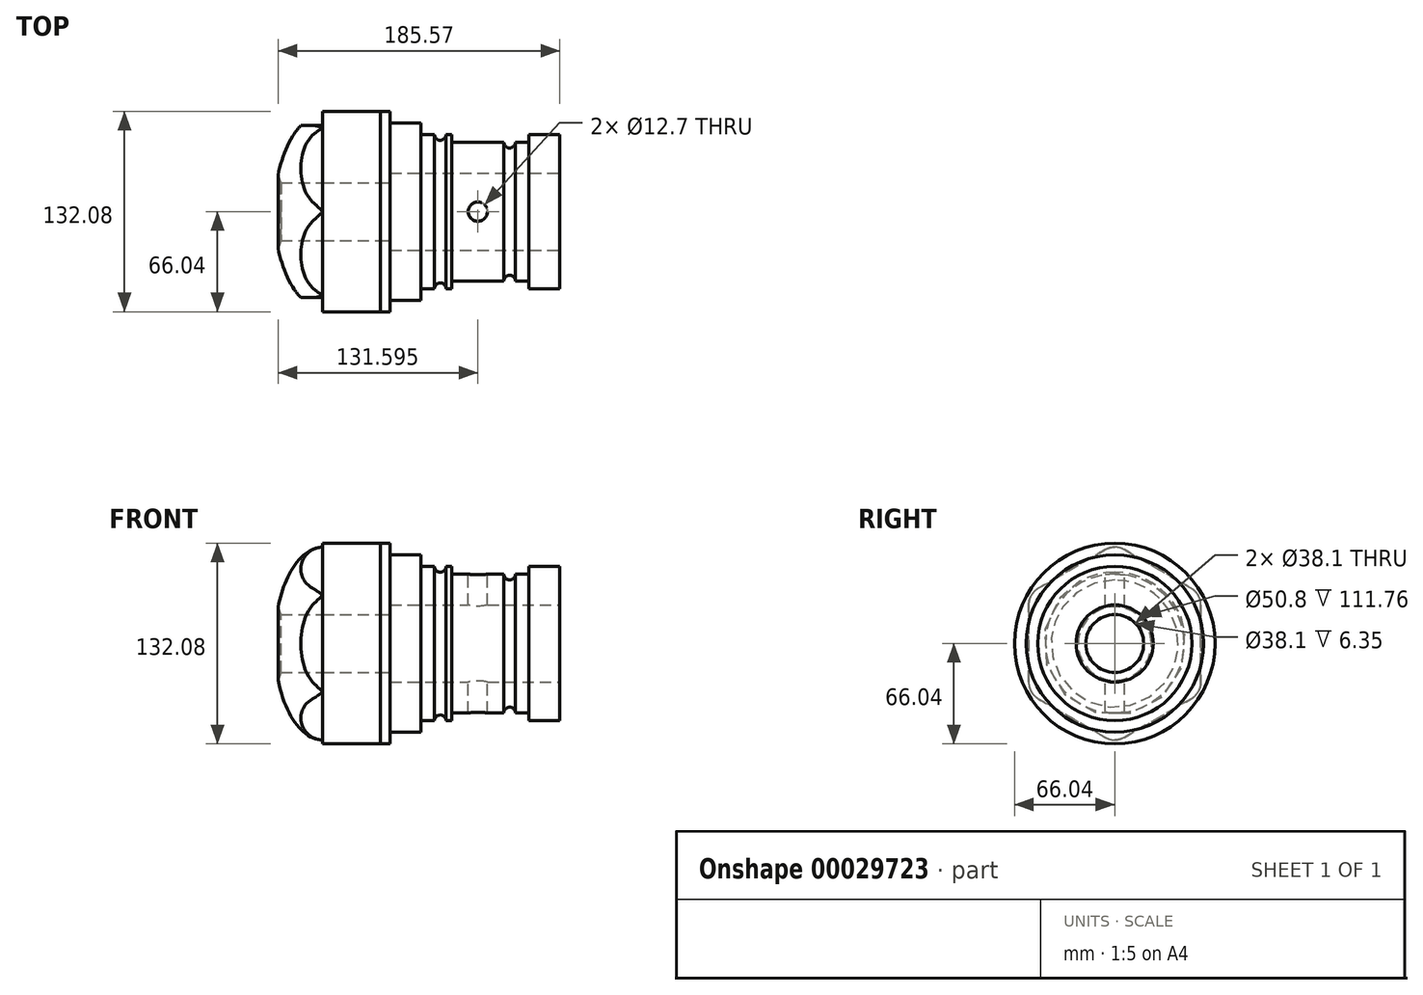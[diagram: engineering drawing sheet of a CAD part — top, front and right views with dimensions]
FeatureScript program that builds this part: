
annotation { "Feature Type Name" : "Feature", "Feature Type Description" : "" }
export const myFeature = defineFeature(function(context is Context, id is Id, definition is map)
    precondition{}
    {
        {
            var Q0;
            Q0=qCreatedBy(makeId("Top.planeOp"),FACE);
            var sketch = newSketch(context, id + "F0", { "sketchPlane" : qUnion([Q0])});
            skLineSegment(sketch, "E0", {"start": v(0, 0) * mm, "end": v(0, -50.8) * mm});
            skLineSegment(sketch, "E1", {"start": v(0, -50.8) * mm, "end": v(-20.32, -50.8) * mm});
            skLineSegment(sketch, "E2", {"start": v(-20.32, -50.8) * mm, "end": v(-20.32, -45.72) * mm});
            skLineSegment(sketch, "E3", {"start": v(-20.32, -45.72) * mm, "end": v(-29.21, -45.72) * mm});
            skLineSegment(sketch, "E4", {"start": v(-91.44, -50.8) * mm, "end": v(-91.44, -58.42) * mm});
            skLineSegment(sketch, "E5", {"start": v(-91.44, -58.42) * mm, "end": v(-111.76, -58.42) * mm});
            skLineSegment(sketch, "E6", {"start": v(-111.76, -58.42) * mm, "end": v(-111.76, -66.04) * mm});
            skLineSegment(sketch, "E7", {"start": v(-111.76, -66.04) * mm, "end": v(-118.11, -66.04) * mm});
            skLineSegment(sketch, "E8", {"start": v(-118.11, -66.04) * mm, "end": v(-118.11, 0) * mm});
            skLineSegment(sketch, "E9", {"start": v(-118.11, 0) * mm, "end": v(0, 0) * mm});
            skLineSegment(sketch, "E10", {"start": v(-91.44, -50.8) * mm, "end": v(-82.55, -50.8) * mm});
            skLineSegment(sketch, "E11", {"start": v(-71.12, -45.72) * mm, "end": v(-71.12, -50.8) * mm});
            skArc(sketch, "E12", {"start": v(-29.21, -45.72) * mm, "mid": v(-33.02, -41.9) * mm, "end": v(-36.83, -45.72) * mm});
            skArc(sketch, "E13", {"start": v(-74.93, -50.8) * mm, "mid": v(-78.74, -47) * mm, "end": v(-82.55, -50.8) * mm});
            skLineSegment(sketch, "E14.trimOffspring", {"start": v(-74.93, -50.8) * mm, "end": v(-71.12, -50.8) * mm});
            skLineSegment(sketch, "E15.trimOffspring", {"start": v(-36.83, -45.72) * mm, "end": v(-71.12, -45.72) * mm});
            skSolve(sketch);
        }
        {
            var Q0;
            Q0 = qSketchRegion(id + "F0", true);
            var Q1;
            Q1=sQuery(id+"F0.wireOp",EDGE,"E9");
            revolve(context, id + "F1", {"entities" : qUnion([Q0]), "axis" : qUnion([Q1]), "revolveType" : RevolveType.FULL});
        }
        {
            var Q0;
            Q0=makeQuery(id+"F1.opRevolve","SWEPT_FACE",FACE,{"disambiguationData":[OSD([sQuery(id+"F0.wireOp",EDGE,"E8")])]});
            var sketch = newSketch(context, id + "F2", { "sketchPlane" : qUnion([Q0])});
            skCircle(sketch, "E16.0", {"center": v(0, 0) * mm, "radius": 66.04 * mm});
            skSolve(sketch);
        }
        {
            var Q0;
            Q0 = qSketchRegion(id + "F2", true);
            extrude(context, id + "F3", {"entities" : qUnion([Q0]), "depth" : 38.1 * mm});
        }
        {
            var Q0;
            Q0=qCreatedBy(makeId("Top.planeOp"),FACE);
            var sketch = newSketch(context, id + "F4", { "sketchPlane" : qUnion([Q0])});
            skLineSegment(sketch, "E17.0", {"start": v(-156.21, -66.04) * mm, "end": v(-156.21, 0) * mm});
            skEllipticalArc(sketch, "E18", {});
            skLineSegment(sketch, "E19", {"start": v(-156.21, 0) * mm, "end": v(-187.96, 0) * mm});
            skPoint(sketch, "E20.orphan", {"position": v(-156.21, 66.04) * mm});
            const initialGuessF4  = {"E18": [-0.15621, 0, 0, -1, 0.0635, 0.03175, 4.71238898038469, 0]};
            skSetInitialGuess(sketch, initialGuessF4);
            skSolve(sketch);
        }
        {
            var Q0;
            Q0 = qSketchRegion(id + "F4", true);
            var Q1;
            Q1=sQuery(id+"F4.wireOp",EDGE,"E19");
            revolve(context, id + "F5", {"entities" : qUnion([Q0]), "axis" : qUnion([Q1]), "revolveType" : RevolveType.FULL});
        }
        {
            var Q0;
            Q0=makeQuery(id+"F3.opExtrude","CAP_FACE",FACE,{"disambiguationData":[OSD([sQuery(id+"F2.wireOp",EDGE,"E16.0")])],"isStart":false});
            var sketch = newSketch(context, id + "F6", { "sketchPlane" : qUnion([Q0])});
            skCircle(sketch, "E21.0", {"center": v(0, 0) * mm, "radius": 66.04 * mm});
            skCircle(sketch, "E22.cCircle", {"center": v(0, 0) * mm, "radius": 65.46 * mm, "construction": true});
            skLineSegment(sketch, "E22.0", {"start": v(6.35, 61.8) * mm, "end": v(50.34, 36.4) * mm});
            skLineSegment(sketch, "E22.1", {"start": v(56.7, 25.4) * mm, "end": v(56.7, -25.4) * mm});
            skLineSegment(sketch, "E22.2", {"start": v(50.34, -36.4) * mm, "end": v(6.35, -61.8) * mm});
            skLineSegment(sketch, "E22.3", {"start": v(-6.35, -61.8) * mm, "end": v(-50.34, -36.4) * mm});
            skLineSegment(sketch, "E22.4", {"start": v(-56.7, -25.4) * mm, "end": v(-56.7, 25.4) * mm});
            skLineSegment(sketch, "E22.5", {"start": v(-50.34, 36.4) * mm, "end": v(-6.35, 61.8) * mm});
            skPoint(sketch, "E23.visualSharp", {"position": v(0, 65.46) * mm});
            skArc(sketch, "E23.filletArc", {"start": v(6.35, 61.8) * mm, "mid": v(0, 63.5) * mm, "end": v(-6.35, 61.8) * mm});
            skPoint(sketch, "E24.visualSharp", {"position": v(56.7, 32.73) * mm});
            skArc(sketch, "E24.filletArc", {"start": v(56.7, 25.4) * mm, "mid": v(55, 31.75) * mm, "end": v(50.34, 36.4) * mm});
            skPoint(sketch, "E25.visualSharp", {"position": v(56.7, -32.73) * mm});
            skArc(sketch, "E25.filletArc", {"start": v(50.34, -36.4) * mm, "mid": v(55, -31.75) * mm, "end": v(56.7, -25.4) * mm});
            skPoint(sketch, "E26.visualSharp", {"position": v(0, -65.46) * mm});
            skArc(sketch, "E26.filletArc", {"start": v(-6.35, -61.8) * mm, "mid": v(0, -63.5) * mm, "end": v(6.35, -61.8) * mm});
            skPoint(sketch, "E27.visualSharp", {"position": v(-56.7, -32.73) * mm});
            skArc(sketch, "E27.filletArc", {"start": v(-56.7, -25.4) * mm, "mid": v(-55, -31.75) * mm, "end": v(-50.34, -36.4) * mm});
            skPoint(sketch, "E28.visualSharp", {"position": v(-56.7, 32.73) * mm});
            skArc(sketch, "E28.filletArc", {"start": v(-50.34, 36.4) * mm, "mid": v(-55, 31.75) * mm, "end": v(-56.7, 25.4) * mm});
            skSolve(sketch);
        }
        {
            var Q0;
            {var subQ16=sQuery(id+"F6.wireOp",EDGE,"E22.0");Q0=makeQuery(id+"F6.imprint","IMPRINT",FACE,{"disambiguationData":[TD([[makeQuery(id+"F6.imprint","IMPRINT",EDGE,{"derivedFrom":subQ16}),-1.0]])]});}
            extrude(context, id + "F7", {"entities" : qUnion([Q0]), "endBound" : BoundingType.SYMMETRIC, "depth" : 127 * mm});
        }
        {
            var Q0;
            Q0=makeQuery(id+"F5.opRevolve","SWEPT_BODY",BODY,{"disambiguationData":[OSD([sQuery(id+"F4.wireOp",EDGE,"E17.0"),sQuery(id+"F4.wireOp",EDGE,"E18"),sQuery(id+"F4.wireOp",EDGE,"E19")])]});
            var Q1;
            Q1=makeQuery(id+"F7.opExtrude","SWEPT_BODY",BODY,{"disambiguationData":[OSD([sQuery(id+"F6.wireOp",EDGE,"E22.0"),sQuery(id+"F6.wireOp",EDGE,"E22.1"),sQuery(id+"F6.wireOp",EDGE,"E22.2"),sQuery(id+"F6.wireOp",EDGE,"E22.3"),sQuery(id+"F6.wireOp",EDGE,"E22.4"),sQuery(id+"F6.wireOp",EDGE,"E22.5"),sQuery(id+"F6.wireOp",EDGE,"E23.filletArc"),sQuery(id+"F6.wireOp",EDGE,"E24.filletArc"),sQuery(id+"F6.wireOp",EDGE,"E25.filletArc"),sQuery(id+"F6.wireOp",EDGE,"E26.filletArc"),sQuery(id+"F6.wireOp",EDGE,"E27.filletArc"),sQuery(id+"F6.wireOp",EDGE,"E28.filletArc")])]});
            booleanBodies(context, id + "F8", {"operationType" : BooleanOperationType.INTERSECTION, "tools" : qUnion([Q0, Q1])});
        }
        {
            var Q0;
            Q0=makeQuery(id+"F1.opRevolve","SWEPT_FACE",FACE,{"disambiguationData":[OSD([sQuery(id+"F0.wireOp",EDGE,"E0")])]});
            var sketch = newSketch(context, id + "F9", { "sketchPlane" : qUnion([Q0])});
            skCircle(sketch, "E29", {"center": v(0, 0) * mm, "radius": 25.4 * mm});
            skSolve(sketch);
        }
        {
            var Q0;
            Q0=makeQuery(id+"F1.opRevolve","SWEPT_FACE",FACE,{"disambiguationData":[OSD([sQuery(id+"F0.wireOp",EDGE,"E6")])]});
            cPlane(context, id + "F10", {"entities" : qUnion([Q0]), "cplaneType" : CPlaneType.OFFSET, "offset" : 0 * mm, "width" : 152.4 * mm, "height" : 152.4 * mm});
        }
        {
            var Q0;
            Q0=makeQuery(id+"F9.imprint","IMPRINT",FACE,{"disambiguationData":[TD([[makeQuery(id+"F9.imprint","IMPRINT",EDGE,{"derivedFrom":sQuery(id+"F9.wireOp",EDGE,"E29")}),1.0]])]});
            var Q1;
            Q1=qCreatedBy(id+"F10.planeOp",FACE);
            extrude(context, id + "F11", {"entities" : qUnion([Q0]), "operationType" : NewBodyOperationType.REMOVE, "endBound" : BoundingType.UP_TO_SURFACE, "oppositeDirection" : true, "endBoundEntityFace" : qUnion([Q1]), "depth" : 254 * mm});
        }
        {
            var Q0;
            Q0=qCreatedBy(id+"F10.planeOp",FACE);
            var sketch = newSketch(context, id + "F12", { "sketchPlane" : qUnion([Q0])});
            skCircle(sketch, "E30.0", {"center": v(0, 0) * mm, "radius": 25.4 * mm, "construction": true});
            skCircle(sketch, "E31", {"center": v(0, 0) * mm, "radius": 19.05 * mm});
            skSolve(sketch);
        }
        {
            var Q0;
            Q0 = qSketchRegion(id + "F12", true);
            extrude(context, id + "F13", {"entities" : qUnion([Q0]), "operationType" : NewBodyOperationType.REMOVE, "endBound" : BoundingType.THROUGH_ALL, "oppositeDirection" : true, "depth" : 25.4 * mm});
        }
        {
            var Q0;
            Q0=makeQuery(id+"F13.boolean.opBoolean","INTERSECT",EDGE,{"derivedFrom":[makeQuery(id+"F5.opRevolve","SWEPT_FACE",FACE,{"disambiguationData":[OSD([sQuery(id+"F4.wireOp",EDGE,"E18")])]}),makeQuery(id+"F13.opExtrude","SWEPT_FACE",FACE,{"disambiguationData":[OSD([sQuery(id+"F12.wireOp",EDGE,"E31")])]})]});
            var Q1;
            Q1=makeQuery(id+"F11.boolean.opBoolean","COPY",EDGE,{"derivedFrom":makeQuery(id+"F11.opExtrude","CAP_EDGE",EDGE,{"disambiguationData":[OSD([sQuery(id+"F9.wireOp",EDGE,"E29")])],"isStart":true})});
            chamfer(context, id + "F14", {"entities" : qUnion([Q0, Q1]), "chamferType" : ChamferType.OFFSET_ANGLE, "width" : 5.08 * mm, "oppositeDirection" : false, "angle" : 30 * degree, "tangentPropagation" : true});
        }
        {
            var Q0;
            Q0=qCreatedBy(makeId("Top.planeOp"),FACE);
            var sketch = newSketch(context, id + "F15", { "sketchPlane" : qUnion([Q0])});
            skLineSegment(sketch, "E32.0", {"start": v(-36.83, -45.72) * mm, "end": v(-36.83, 45.72) * mm, "construction": true});
            skLineSegment(sketch, "E33.0", {"start": v(-71.12, -45.72) * mm, "end": v(-71.12, 45.72) * mm, "construction": true});
            skLineSegment(sketch, "E34", {"start": v(-71.12, 0) * mm, "end": v(-36.83, 0) * mm, "construction": true});
            skCircle(sketch, "E35", {"center": v(-53.98, 0) * mm, "radius": 6.35 * mm});
            skSolve(sketch);
        }
        {
            var Q0;
            Q0=makeQuery(id+"F15.imprint","IMPRINT",FACE,{"disambiguationData":[TD([[makeQuery(id+"F15.imprint","IMPRINT",EDGE,{"derivedFrom":sQuery(id+"F15.wireOp",EDGE,"E35")}),1.0]])]});
            extrude(context, id + "F16", {"entities" : qUnion([Q0]), "operationType" : NewBodyOperationType.REMOVE, "endBound" : BoundingType.SYMMETRIC, "oppositeDirection" : true, "depth" : 127 * mm});
        }
    });
